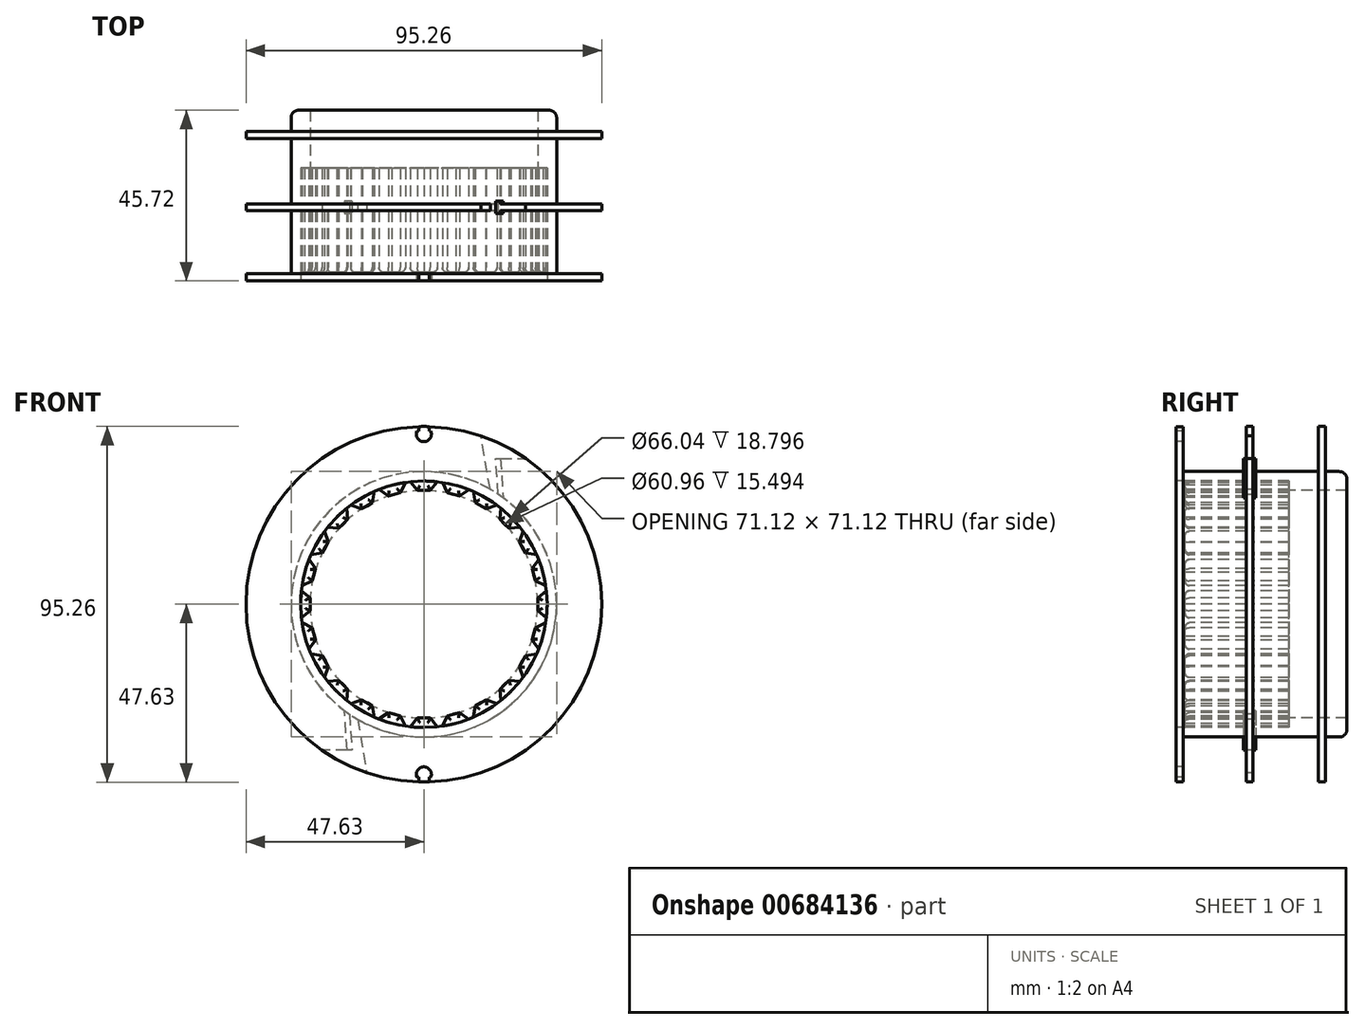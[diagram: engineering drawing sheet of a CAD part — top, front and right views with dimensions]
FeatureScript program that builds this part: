
annotation { "Feature Type Name" : "Feature", "Feature Type Description" : "" }
export const myFeature = defineFeature(function(context is Context, id is Id, definition is map)
    precondition{}
    {
        {
            var Q0;
            Q0=qCreatedBy(makeId("Front.planeOp"),FACE);
            var sketch = newSketch(context, id + "F0", { "sketchPlane" : qUnion([Q0])});
            skCircle(sketch, "E0", {"center": v(0, 0) * mm, "radius": 33.02 * mm});
            skCircle(sketch, "E1", {"center": v(0, 0) * mm, "radius": 30.48 * mm});
            skLineSegment(sketch, "E2", {"start": v(0, 30.48) * mm, "end": v(0, 33.02) * mm, "construction": true});
            skLineSegment(sketch, "E3", {"start": v(-1.7, 30.48) * mm, "end": v(1.7, 30.48) * mm});
            skLineSegment(sketch, "E4", {"start": v(-3.66, 33.02) * mm, "end": v(3.66, 33.02) * mm});
            skLineSegment(sketch, "E5", {"start": v(-3.66, 33.02) * mm, "end": v(-3.66, 24.87) * mm, "construction": true});
            skLineSegment(sketch, "E6", {"start": v(3.66, 33.02) * mm, "end": v(3.66, 24.07) * mm, "construction": true});
            skArc(sketch, "E7", {"start": v(-1.7, 30.48) * mm, "mid": v(0, 30.48) * mm, "end": v(1.7, 30.48) * mm});
            skLineSegment(sketch, "E8", {"start": v(-1.7, 30.48) * mm, "end": v(-3.66, 32.82) * mm});
            skLineSegment(sketch, "E9", {"start": v(1.7, 30.48) * mm, "end": v(3.66, 32.8) * mm});
            skArc(sketch, "E10", {"start": v(3.66, 32.8) * mm, "mid": v(0, 33.02) * mm, "end": v(-3.66, 32.82) * mm});
            skSolve(sketch);
        }
        {
            var Q0;
            {var subQ4=sQuery(id+"F0.wireOp",EDGE,"E8");Q0=makeQuery(id+"F0.imprint","IMPRINT",FACE,{"disambiguationData":[TD([[makeQuery(id+"F0.imprint","IMPRINT",EDGE,{"derivedFrom":subQ4}),-1.0]])]});}
            extrude(context, id + "F1", {"entities" : qUnion([Q0]), "oppositeDirection" : true, "depth" : 27.94 * mm, "offsetDistance" : 25.4 * mm});
        }
        {
            var Q0;
            Q0=qCreatedBy(makeId("Right.planeOp"),FACE);
            var sketch = newSketch(context, id + "F2", { "sketchPlane" : qUnion([Q0])});
            skLineSegment(sketch, "E11", {"start": v(0, 0) * mm, "end": v(-58.04, 0) * mm, "construction": true});
            skSolve(sketch);
        }
        {
            var Q0;
            Q0=makeQuery(id+"F1.opExtrude","CAP_EDGE",EDGE,{"disambiguationData":[OSD([sQuery(id+"F0.wireOp",EDGE,"E8")])],"isStart":true});
            var Q1;
            Q1=makeQuery(id+"F1.opExtrude","CAP_EDGE",EDGE,{"disambiguationData":[OSD([sQuery(id+"F0.wireOp",EDGE,"E3")])],"isStart":true});
            var Q2;
            Q2=makeQuery(id+"F1.opExtrude","CAP_EDGE",EDGE,{"disambiguationData":[OSD([sQuery(id+"F0.wireOp",EDGE,"E9")])],"isStart":true});
            fillet(context, id + "F3", {"entities" : qUnion([Q0, Q1, Q2]), "radius" : 1.27 * mm, "tangentPropagation" : true, "allowEdgeOverflow" : false});
        }
        {
            var Q0;
            Q0=makeQuery(id+"F1.opExtrude","SWEPT_BODY",BODY,{"disambiguationData":[OSD([sQuery(id+"F0.wireOp",EDGE,"E0"),sQuery(id+"F0.wireOp",EDGE,"E3"),sQuery(id+"F0.wireOp",EDGE,"E8"),sQuery(id+"F0.wireOp",EDGE,"E9"),sQuery(id+"F0.wireOp",EDGE,"E10")])]});
            var Q1;
            Q1=sQuery(id+"F2.wireOp",EDGE,"E11");
            circularPattern(context, id + "F4", {"entities" : qUnion([Q0]), "axis" : qUnion([Q1]), "angle" : 360 * degree, "instanceCount" : 24, "equalSpace" : true});
        }
        {
            var Q0;
            Q0=qCreatedBy(makeId("Front.planeOp"),FACE);
            cPlane(context, id + "F5", {"entities" : qUnion([Q0]), "cplaneType" : CPlaneType.OFFSET, "offset" : 2.3 * mm, "width" : 152.4 * mm, "height" : 152.4 * mm});
        }
        {
            var Q0;
            Q0=qCreatedBy(id+"F5.planeOp",FACE);
            var sketch = newSketch(context, id + "F6", { "sketchPlane" : qUnion([Q0])});
            skCircle(sketch, "E12.1", {"center": v(0, 0) * mm, "radius": 33.02 * mm});
            skCircle(sketch, "E13", {"center": v(0, 0) * mm, "radius": 35.56 * mm});
            skArc(sketch, "E14", {"start": v(-1.4, 47.6) * mm, "mid": v(0, -47.62) * mm, "end": v(1.4, 47.6) * mm});
            skLineSegment(sketch, "E15", {"start": v(0, 47.63) * mm, "end": v(0, 43.56) * mm, "construction": true});
            skLineSegment(sketch, "E16", {"start": v(0, 43.56) * mm, "end": v(0, 46.36) * mm, "construction": true});
            skArc(sketch, "E17", {"start": v(-1.88, 46.36) * mm, "mid": v(0, 43.56) * mm, "end": v(1.88, 46.36) * mm});
            skLineSegment(sketch, "E18", {"start": v(-1.88, 46.36) * mm, "end": v(-1.4, 46.36) * mm});
            skLineSegment(sketch, "E19", {"start": v(1.4, 46.36) * mm, "end": v(1.4, 47.6) * mm});
            skLineSegment(sketch, "E20", {"start": v(-1.4, 46.36) * mm, "end": v(-1.4, 47.6) * mm});
            skPoint(sketch, "E21.orphan", {"position": v(-3.32, 46.36) * mm});
            skLineSegment(sketch, "E22.trimOffspring", {"start": v(1.4, 46.36) * mm, "end": v(1.88, 46.36) * mm});
            skLineSegment(sketch, "E23", {"start": v(0, 0) * mm, "end": v(16.3, 0) * mm, "construction": true});
            skLineSegment(sketch, "E24.MirrorCS", {"start": v(1.4, -46.36) * mm, "end": v(1.88, -46.36) * mm});
            skLineSegment(sketch, "E25.MirrorCS", {"start": v(1.4, -46.36) * mm, "end": v(1.4, -47.6) * mm});
            skLineSegment(sketch, "E26.MirrorCS", {"start": v(-1.88, -46.36) * mm, "end": v(-1.4, -46.36) * mm});
            skLineSegment(sketch, "E27.MirrorCS", {"start": v(-1.4, -46.36) * mm, "end": v(-1.4, -47.6) * mm});
            skLineSegment(sketch, "E28.MirrorCS", {"start": v(0, -47.63) * mm, "end": v(0, -43.56) * mm, "construction": true});
            skLineSegment(sketch, "E29.MirrorCS", {"start": v(0, -43.56) * mm, "end": v(0, -46.36) * mm, "construction": true});
            skPoint(sketch, "E30.MirrorP", {"position": v(-3.32, -46.36) * mm});
            skArc(sketch, "E31.MirrorCS", {"start": v(-1.88, -46.36) * mm, "mid": v(0, -43.56) * mm, "end": v(1.88, -46.36) * mm});
            skSolve(sketch);
        }
        {
            var Q0;
            Q0=makeQuery(id+"F6.imprint","IMPRINT",FACE,{"disambiguationData":[TD([[makeQuery(id+"F6.imprint","IMPRINT",EDGE,{"derivedFrom":sQuery(id+"F6.wireOp",EDGE,"E12.1")}),-1.0]])]});
            extrude(context, id + "F7", {"entities" : qUnion([Q0]), "operationType" : NewBodyOperationType.ADD, "oppositeDirection" : true, "depth" : 45.72 * mm, "offsetDistance" : 25.4 * mm});
        }
        {
            var Q0;
            Q0=makeQuery(id+"F4.opPattern","COPY",FACE,{"derivedFrom":makeQuery(id+"F1.opExtrude","CAP_FACE",FACE,{"disambiguationData":[OSD([sQuery(id+"F0.wireOp",EDGE,"E0"),sQuery(id+"F0.wireOp",EDGE,"E3"),sQuery(id+"F0.wireOp",EDGE,"E8"),sQuery(id+"F0.wireOp",EDGE,"E9"),sQuery(id+"F0.wireOp",EDGE,"E10")])],"isStart":false}),"instanceName":"4"});
            cPlane(context, id + "F8", {"entities" : qUnion([Q0]), "cplaneType" : CPlaneType.OFFSET, "offset" : 0 * mm, "width" : 152.4 * mm, "height" : 152.4 * mm});
        }
        {
            var Q0;
            Q0=qCreatedBy(id+"F8.planeOp",FACE);
            var sketch = newSketch(context, id + "F9", { "sketchPlane" : qUnion([Q0])});
            skCircle(sketch, "E32.0", {"center": v(0, 0) * mm, "radius": 30.48 * mm});
            skCircle(sketch, "E33.0", {"center": v(0, 0) * mm, "radius": 33.02 * mm});
            skSolve(sketch);
        }
        {
            var Q0;
            Q0 = qSketchRegion(id + "F9", true);
            var Q1;
            Q1=makeQuery(id+"F7.opExtrude","CAP_FACE",FACE,{"disambiguationData":[OSD([sQuery(id+"F6.wireOp",EDGE,"E12.1"),sQuery(id+"F6.wireOp",EDGE,"E13")])],"isStart":false});
            extrude(context, id + "F10", {"entities" : qUnion([Q0]), "operationType" : NewBodyOperationType.ADD, "endBound" : BoundingType.UP_TO_SURFACE, "depth" : 25.4 * mm, "endBoundEntityFace" : qUnion([Q1]), "offsetDistance" : 25.4 * mm});
        }
        {
            var Q0;
            Q0=makeQuery(id+"F7.opExtrude","CAP_EDGE",EDGE,{"disambiguationData":[OSD([sQuery(id+"F6.wireOp",EDGE,"E13")])],"isStart":false});
            fillet(context, id + "F11", {"entities" : qUnion([Q0]), "radius" : 2.03 * mm, "tangentPropagation" : true, "allowEdgeOverflow" : false});
        }
        {
            var Q0;
            Q0=makeQuery(id+"F6.imprint","IMPRINT",FACE,{"disambiguationData":[TD([[makeQuery(id+"F6.imprint","IMPRINT",EDGE,{"derivedFrom":sQuery(id+"F6.wireOp",EDGE,"E13")}),-1.0]])]});
            extrude(context, id + "F12", {"entities" : qUnion([Q0]), "operationType" : NewBodyOperationType.ADD, "oppositeDirection" : true, "depth" : 1.9 * mm, "offsetDistance" : 25.4 * mm});
        }
        {
            var Q0;
            {var subQ0=sQuery(id+"F6.wireOp",EDGE,"E13");var subQ1=sQuery(id+"F6.wireOp",EDGE,"E12.1");Q0=makeQuery(id+"F10.boolean.opBoolean","MERGE",FACE,{"derivedFrom":[makeQuery(id+"F7.opExtrude","CAP_FACE",FACE,{"disambiguationData":[OSD([subQ1,subQ0])],"isStart":false}),makeQuery(id+"F10.opExtrude","CAP_FACE",FACE,{"disambiguationData":[OSD([subQ1,subQ0])],"isStart":false})]});}
            cPlane(context, id + "F13", {"entities" : qUnion([Q0]), "cplaneType" : CPlaneType.OFFSET, "offset" : 5.7 * mm, "oppositeDirection" : true, "width" : 152.4 * mm, "height" : 152.4 * mm});
        }
        {
            var Q0;
            Q0=qCreatedBy(id+"F13.planeOp",FACE);
            var sketch = newSketch(context, id + "F14", { "sketchPlane" : qUnion([Q0])});
            skCircle(sketch, "E34.0", {"center": v(0, 0) * mm, "radius": 47.63 * mm});
            skCircle(sketch, "E35.0", {"center": v(0, 0) * mm, "radius": 35.56 * mm});
            skSolve(sketch);
        }
        {
            var Q0;
            Q0 = qSketchRegion(id + "F14", true);
            extrude(context, id + "F15", {"entities" : qUnion([Q0]), "operationType" : NewBodyOperationType.ADD, "oppositeDirection" : true, "depth" : 1.9 * mm, "offsetDistance" : 25.4 * mm});
        }
        {
            var Q0;
            Q0=makeQuery(id+"F15.opExtrude","CAP_FACE",FACE,{"disambiguationData":[OSD([sQuery(id+"F14.wireOp",EDGE,"E34.0"),sQuery(id+"F14.wireOp",EDGE,"E35.0")])],"isStart":true});
            cPlane(context, id + "F16", {"entities" : qUnion([Q0]), "cplaneType" : CPlaneType.OFFSET, "offset" : 21.2 * mm, "oppositeDirection" : true, "width" : 152.4 * mm, "height" : 152.4 * mm});
        }
        {
            var Q0;
            Q0=qCreatedBy(id+"F16.planeOp",FACE);
            var sketch = newSketch(context, id + "F17", { "sketchPlane" : qUnion([Q0])});
            skArc(sketch, "E36.0", {"start": v(-15.26, 45.12) * mm, "mid": v(42.53, 21.43) * mm, "end": v(27.19, -39.1) * mm});
            skCircle(sketch, "E36.1", {"center": v(0, 0) * mm, "radius": 35.56 * mm});
            skLineSegment(sketch, "E37", {"start": v(0, 55.44) * mm, "end": v(0, -63.33) * mm, "construction": true});
            skLineSegment(sketch, "E38", {"start": v(0, 0) * mm, "end": v(-27.98, 48.47) * mm, "construction": true});
            skLineSegment(sketch, "E39", {"start": v(-17.78, 30.8) * mm, "end": v(-15.26, 45.12) * mm});
            skPoint(sketch, "E39.endSnap0", {"position": v(-14, 24.23) * mm});
            skPoint(sketch, "E40.orphan", {"position": v(-14, 52.29) * mm});
            skLineSegment(sketch, "E41", {"start": v(-19.93, 29.45) * mm, "end": v(-19.26, 39.1) * mm});
            skLineSegment(sketch, "E42.0", {"start": v(-21.27, 28.5) * mm, "end": v(-20.53, 39.1) * mm});
            skLineSegment(sketch, "E43", {"start": v(-19.26, 39.1) * mm, "end": v(-27.19, 39.1) * mm});
            skLineSegment(sketch, "E44", {"start": v(0, 0) * mm, "end": v(-26.94, -15.55) * mm, "construction": true});
            skPoint(sketch, "E45.MirrorP", {"position": v(14, -24.23) * mm});
            skLineSegment(sketch, "E46.MirrorCS", {"start": v(19.93, -29.45) * mm, "end": v(19.26, -39.1) * mm});
            skLineSegment(sketch, "E47.MirrorCS", {"start": v(21.27, -28.5) * mm, "end": v(20.53, -39.1) * mm});
            skLineSegment(sketch, "E48.MirrorCS", {"start": v(19.26, -39.1) * mm, "end": v(27.19, -39.1) * mm});
            skLineSegment(sketch, "E49.MirrorCS", {"start": v(17.78, -30.8) * mm, "end": v(15.26, -45.12) * mm});
            skArc(sketch, "E50.trimOffspring", {"start": v(15.26, -45.12) * mm, "mid": v(-42.53, -21.43) * mm, "end": v(-27.19, 39.1) * mm});
            skSolve(sketch);
        }
        {
            var Q0;
            Q0 = qSketchRegion(id + "F17", true);
            extrude(context, id + "F18", {"entities" : qUnion([Q0]), "operationType" : NewBodyOperationType.ADD, "depth" : 1.78 * mm, "offsetDistance" : 25.4 * mm});
        }
        {
            var Q0;
            {var subQ0=sQuery(id+"F17.wireOp",EDGE,"E41");Q0=makeQuery(id+"F17.imprint","IMPRINT",FACE,{"disambiguationData":[TD([[makeQuery(id+"F17.imprint","IMPRINT",EDGE,{"derivedFrom":subQ0}),1.0]])]});}
            extrude(context, id + "F19", {"entities" : qUnion([Q0]), "operationType" : NewBodyOperationType.ADD, "depth" : 2.54 * mm, "offsetDistance" : 25.4 * mm, "hasSecondDirection" : true, "secondDirectionOppositeDirection" : false, "secondDirectionDepth" : -0.76 * mm});
        }
        {
            var Q0;
            {var subQ0=sQuery(id+"F17.wireOp",EDGE,"E47.MirrorCS");Q0=makeQuery(id+"F17.imprint","IMPRINT",FACE,{"disambiguationData":[TD([[makeQuery(id+"F17.imprint","IMPRINT",EDGE,{"derivedFrom":subQ0}),-1.0]])]});}
            extrude(context, id + "F20", {"entities" : qUnion([Q0]), "operationType" : NewBodyOperationType.ADD, "depth" : 2.54 * mm, "offsetDistance" : 25.4 * mm, "hasSecondDirection" : true, "secondDirectionOppositeDirection" : false, "secondDirectionDepth" : -0.76 * mm});
        }
    });
